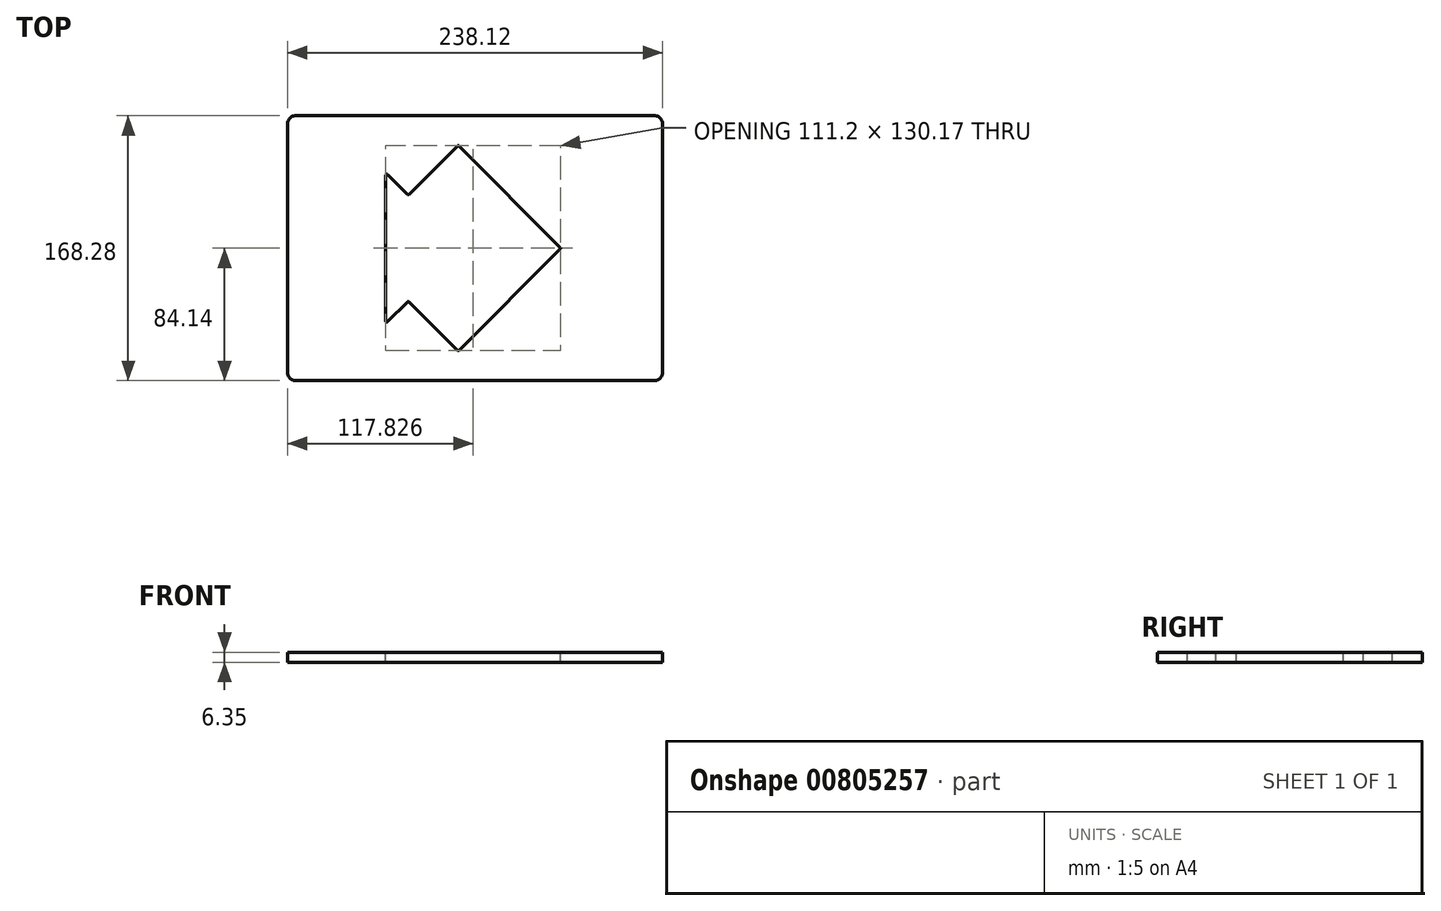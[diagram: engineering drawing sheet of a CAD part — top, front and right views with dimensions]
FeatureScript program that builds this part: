
annotation { "Feature Type Name" : "Feature", "Feature Type Description" : "" }
export const myFeature = defineFeature(function(context is Context, id is Id, definition is map)
    precondition{}
    {
        {
            var Q0;
            Q0=qCreatedBy(makeId("Top.planeOp"),FACE);
            var sketch = newSketch(context, id + "F0", { "sketchPlane" : qUnion([Q0])});
            skLineSegment(sketch, "E0.bottom", {"start": v(119.06, -84.14) * mm, "end": v(-119.06, -84.14) * mm});
            skLineSegment(sketch, "E0.top", {"start": v(119.06, 84.14) * mm, "end": v(-119.06, 84.14) * mm});
            skLineSegment(sketch, "E0.left", {"start": v(119.06, -84.14) * mm, "end": v(119.06, 84.14) * mm});
            skLineSegment(sketch, "E0.right", {"start": v(-119.06, -84.14) * mm, "end": v(-119.06, 84.14) * mm});
            skPoint(sketch, "E0.middle", {"position": v(0, 0) * mm});
            skSolve(sketch);
        }
        {
            var Q0;
            Q0 = qSketchRegion(id + "F0", true);
            extrude(context, id + "F1", {"entities" : qUnion([Q0]), "depth" : 6.35 * mm, "offsetDistance" : 25.4 * mm});
        }
        {
            var Q0;
            Q0=makeQuery(id+"F1.opExtrude","CAP_FACE",FACE,{"disambiguationData":[OSD([sQuery(id+"F0.wireOp",EDGE,"E0.bottom"),sQuery(id+"F0.wireOp",EDGE,"E0.top"),sQuery(id+"F0.wireOp",EDGE,"E0.left"),sQuery(id+"F0.wireOp",EDGE,"E0.right")])],"isStart":false});
            var sketch = newSketch(context, id + "F2", { "sketchPlane" : qUnion([Q0])});
            skLineSegment(sketch, "E1", {"start": v(-55.56, 44.96) * mm, "end": v(-55.56, 0) * mm});
            skLineSegment(sketch, "E2", {"start": v(-55.56, 44.96) * mm, "end": v(-42.46, 31.84) * mm});
            skLineSegment(sketch, "E3", {"start": v(-42.46, 31.84) * mm, "end": v(-10.65, 63.61) * mm});
            skLineSegment(sketch, "E4", {"start": v(-10.65, 63.61) * mm, "end": v(52.9, 0) * mm});
            skLineSegment(sketch, "E5.MirrorCS", {"start": v(-55.56, -44.96) * mm, "end": v(-55.56, 0) * mm});
            skLineSegment(sketch, "E6.MirrorCS", {"start": v(-55.56, -44.96) * mm, "end": v(-42.46, -31.84) * mm});
            skLineSegment(sketch, "E7.MirrorCS", {"start": v(-42.46, -31.84) * mm, "end": v(-10.65, -63.61) * mm});
            skLineSegment(sketch, "E8.MirrorCS", {"start": v(-10.65, -63.61) * mm, "end": v(52.9, 0) * mm});
            skSolve(sketch);
        }
        {
            var Q0;
            Q0 = qSketchRegion(id + "F2", true);
            extrude(context, id + "F3", {"entities" : qUnion([Q0]), "operationType" : NewBodyOperationType.REMOVE, "oppositeDirection" : true, "depth" : 25.4 * mm, "offsetDistance" : 25.4 * mm});
        }
        {
            var Q0;
            Q0=makeQuery(id+"F1.opExtrude","SWEPT_EDGE",EDGE,{"disambiguationData":[OSD([sQuery(id+"F0.wireOp",EDGE,"E0.bottom"),sQuery(id+"F0.wireOp",EDGE,"E0.left")])]});
            var Q1;
            Q1=makeQuery(id+"F1.opExtrude","SWEPT_EDGE",EDGE,{"disambiguationData":[OSD([sQuery(id+"F0.wireOp",EDGE,"E0.top"),sQuery(id+"F0.wireOp",EDGE,"E0.left")])]});
            var Q2;
            Q2=makeQuery(id+"F1.opExtrude","SWEPT_EDGE",EDGE,{"disambiguationData":[OSD([sQuery(id+"F0.wireOp",EDGE,"E0.bottom"),sQuery(id+"F0.wireOp",EDGE,"E0.right")])]});
            var Q3;
            Q3=makeQuery(id+"F1.opExtrude","SWEPT_EDGE",EDGE,{"disambiguationData":[OSD([sQuery(id+"F0.wireOp",EDGE,"E0.top"),sQuery(id+"F0.wireOp",EDGE,"E0.right")])]});
            fillet(context, id + "F4", {"entities" : qUnion([Q0, Q1, Q2, Q3]), "radius" : 5.08 * mm, "tangentPropagation" : true, "allowEdgeOverflow" : false});
        }
        {
            var Q0;
            Q0=makeQuery(id+"F1.opExtrude","CAP_FACE",FACE,{"disambiguationData":[OSD([sQuery(id+"F0.wireOp",EDGE,"E0.bottom"),sQuery(id+"F0.wireOp",EDGE,"E0.top"),sQuery(id+"F0.wireOp",EDGE,"E0.left"),sQuery(id+"F0.wireOp",EDGE,"E0.right")])],"isStart":false});
            var sketch = newSketch(context, id + "F5", { "sketchPlane" : qUnion([Q0])});
            skLineSegment(sketch, "E9.0", {"start": v(-55.49, 46.68) * mm, "end": v(-43.01, 34.2) * mm});
            skLineSegment(sketch, "E9.1", {"start": v(-56.83, 46.12) * mm, "end": v(-56.83, -46.12) * mm});
            skLineSegment(sketch, "E9.2", {"start": v(-10.1, 64.85) * mm, "end": v(54.13, 0.56) * mm});
            skLineSegment(sketch, "E9.3", {"start": v(-10.1, -64.85) * mm, "end": v(54.13, -0.56) * mm});
            skLineSegment(sketch, "E9.4", {"start": v(-41.9, -34.2) * mm, "end": v(-11.2, -64.85) * mm});
            skLineSegment(sketch, "E9.5", {"start": v(-41.9, 34.2) * mm, "end": v(-11.2, 64.85) * mm});
            skLineSegment(sketch, "E9.6", {"start": v(-55.49, -46.68) * mm, "end": v(-43.01, -34.2) * mm});
            skPoint(sketch, "E10.visualSharp", {"position": v(-10.65, 65.4) * mm});
            skArc(sketch, "E10.filletArc", {"start": v(-10.1, 64.85) * mm, "mid": v(-10.65, 65.08) * mm, "end": v(-11.2, 64.85) * mm});
            skPoint(sketch, "E11.visualSharp", {"position": v(54.7, 0) * mm});
            skArc(sketch, "E11.filletArc", {"start": v(54.13, -0.56) * mm, "mid": v(54.37, 0) * mm, "end": v(54.13, 0.56) * mm});
            skPoint(sketch, "E12.visualSharp", {"position": v(-10.65, -65.4) * mm});
            skArc(sketch, "E12.filletArc", {"start": v(-11.2, -64.85) * mm, "mid": v(-10.65, -65.08) * mm, "end": v(-10.1, -64.85) * mm});
            skPoint(sketch, "E13.visualSharp", {"position": v(-42.46, -33.64) * mm});
            skArc(sketch, "E13.filletArc", {"start": v(-41.9, -34.2) * mm, "mid": v(-42.46, -33.96) * mm, "end": v(-43.01, -34.2) * mm});
            skPoint(sketch, "E14.visualSharp", {"position": v(-56.83, -48.03) * mm});
            skArc(sketch, "E14.filletArc", {"start": v(-56.83, -46.12) * mm, "mid": v(-56.35, -46.85) * mm, "end": v(-55.49, -46.68) * mm});
            skPoint(sketch, "E15.visualSharp", {"position": v(-56.83, 48.03) * mm});
            skArc(sketch, "E15.filletArc", {"start": v(-55.49, 46.68) * mm, "mid": v(-56.35, 46.85) * mm, "end": v(-56.83, 46.12) * mm});
            skPoint(sketch, "E16.visualSharp", {"position": v(-42.46, 33.64) * mm});
            skArc(sketch, "E16.filletArc", {"start": v(-43.01, 34.2) * mm, "mid": v(-42.46, 33.96) * mm, "end": v(-41.9, 34.2) * mm});
            skSolve(sketch);
        }
        {
            var Q0;
            Q0 = qSketchRegion(id + "F5", true);
            extrude(context, id + "F6", {"entities" : qUnion([Q0]), "operationType" : NewBodyOperationType.REMOVE, "endBound" : BoundingType.THROUGH_ALL, "oppositeDirection" : true, "depth" : 25.4 * mm, "offsetDistance" : 25.4 * mm});
        }
    });
